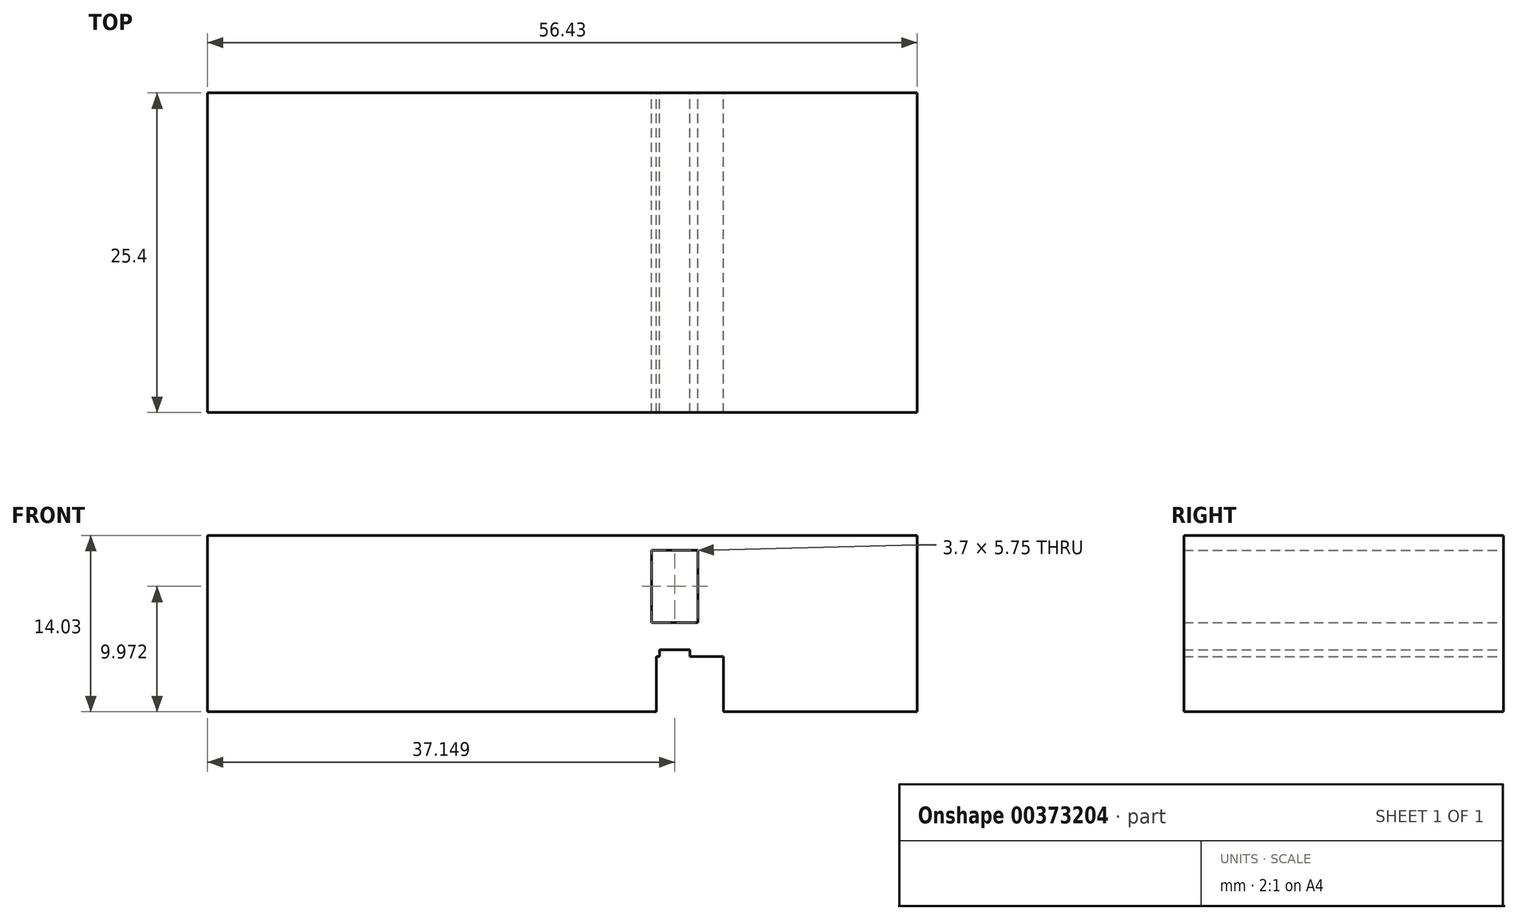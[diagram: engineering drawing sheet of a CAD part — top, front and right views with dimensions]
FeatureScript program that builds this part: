
annotation { "Feature Type Name" : "Feature", "Feature Type Description" : "" }
export const myFeature = defineFeature(function(context is Context, id is Id, definition is map)
    precondition{}
    {
        {
            var Q0;
            Q0=qCreatedBy(makeId("Front.planeOp"),FACE);
            var sketch = newSketch(context, id + "F0", { "sketchPlane" : qUnion([Q0])});
            skLineSegment(sketch, "E0.bottom", {"start": v(-40.8, 29.2) * mm, "end": v(-97.23, 29.2) * mm});
            skLineSegment(sketch, "E0.top", {"start": v(-40.8, 15.17) * mm, "end": v(-97.23, 15.17) * mm});
            skLineSegment(sketch, "E0.left", {"start": v(-40.8, 29.2) * mm, "end": v(-40.8, 15.17) * mm});
            skLineSegment(sketch, "E0.right", {"start": v(-97.23, 29.2) * mm, "end": v(-97.23, 15.17) * mm});
            skPoint(sketch, "E0.middle", {"position": v(-69.01, 22.18) * mm});
            skLineSegment(sketch, "E1.bottom", {"start": v(-61.54, 10.91) * mm, "end": v(-56.2, 10.91) * mm});
            skLineSegment(sketch, "E1.top", {"start": v(-61.54, 19.58) * mm, "end": v(-56.2, 19.58) * mm});
            skLineSegment(sketch, "E1.left", {"start": v(-61.54, 10.91) * mm, "end": v(-61.54, 19.58) * mm});
            skLineSegment(sketch, "E1.right", {"start": v(-56.2, 10.91) * mm, "end": v(-56.2, 19.58) * mm});
            skPoint(sketch, "E1.middle", {"position": v(-58.87, 15.24) * mm});
            skLineSegment(sketch, "E2.bottom", {"start": v(-58.87, 15.24) * mm, "end": v(-61.3, 15.24) * mm});
            skLineSegment(sketch, "E2.top", {"start": v(-58.87, 20.12) * mm, "end": v(-61.3, 20.12) * mm});
            skLineSegment(sketch, "E2.left", {"start": v(-58.87, 15.24) * mm, "end": v(-58.87, 20.12) * mm});
            skLineSegment(sketch, "E2.right", {"start": v(-61.3, 15.24) * mm, "end": v(-61.3, 20.12) * mm});
            skPoint(sketch, "E2.middle", {"position": v(-60.08, 17.68) * mm});
            skLineSegment(sketch, "E3.bottom", {"start": v(-58.23, 22.27) * mm, "end": v(-61.93, 22.27) * mm});
            skLineSegment(sketch, "E3.top", {"start": v(-58.23, 28.02) * mm, "end": v(-61.93, 28.02) * mm});
            skLineSegment(sketch, "E3.left", {"start": v(-58.23, 22.27) * mm, "end": v(-58.23, 28.02) * mm});
            skLineSegment(sketch, "E3.right", {"start": v(-61.93, 22.27) * mm, "end": v(-61.93, 28.02) * mm});
            skPoint(sketch, "E3.middle", {"position": v(-60.08, 25.14) * mm});
            skSolve(sketch);
        }
        {
            var Q0;
            Q0=makeQuery(id+"F0.imprint","IMPRINT",FACE,{"disambiguationData":[TD([[makeQuery(id+"F0.imprint","IMPRINT",EDGE,{"derivedFrom":sQuery(id+"F0.wireOp",EDGE,"E0.bottom")}),1.0]])]});
            extrude(context, id + "F1", {"entities" : qUnion([Q0]), "depth" : 25.4 * mm});
        }
    });
